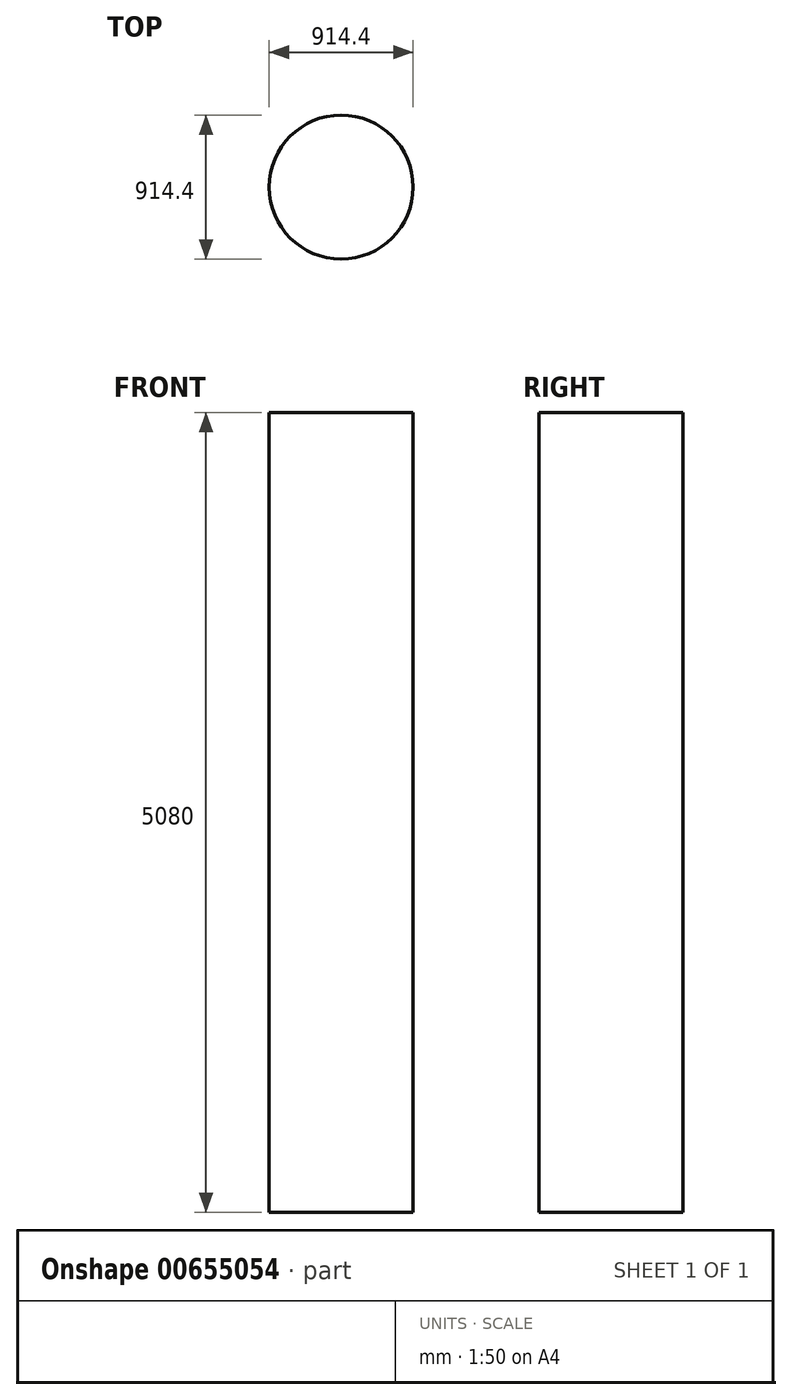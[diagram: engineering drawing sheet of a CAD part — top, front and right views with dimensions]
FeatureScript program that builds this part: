
annotation { "Feature Type Name" : "Feature", "Feature Type Description" : "" }
export const myFeature = defineFeature(function(context is Context, id is Id, definition is map)
    precondition{}
    {
        {
            var Q0;
            Q0=qCreatedBy(makeId("Top.planeOp"),FACE);
            var sketch = newSketch(context, id + "F0", { "sketchPlane" : qUnion([Q0])});
            skCircle(sketch, "E0", {"center": v(0, 0) * mm, "radius": 457.2 * mm});
            skSolve(sketch);
        }
        {
            var Q0;
            Q0=makeQuery(id+"F0.imprint","IMPRINT",FACE,{"disambiguationData":[TD([[makeQuery(id+"F0.imprint","IMPRINT",EDGE,{"derivedFrom":sQuery(id+"F0.wireOp",EDGE,"E0")}),1.0]])]});
            extrude(context, id + "F1", {"entities" : qUnion([Q0]), "depth" : 5080 * mm, "offsetDistance" : 25.4 * mm});
        }
    });
